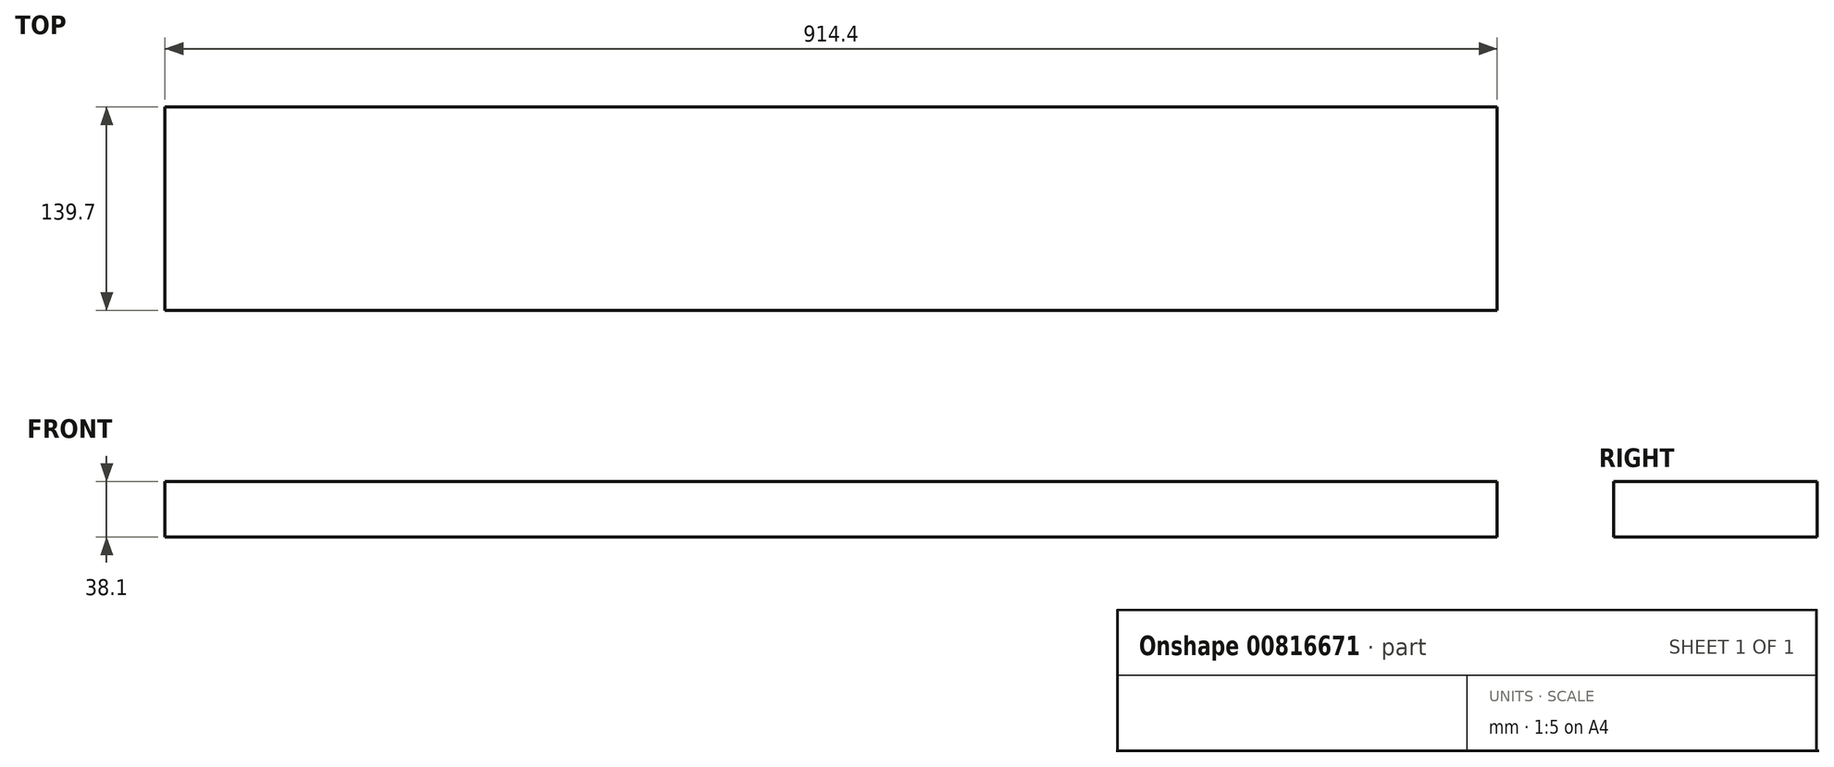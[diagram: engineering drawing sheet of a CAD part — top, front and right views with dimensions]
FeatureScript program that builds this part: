
annotation { "Feature Type Name" : "Feature", "Feature Type Description" : "" }
export const myFeature = defineFeature(function(context is Context, id is Id, definition is map)
    precondition{}
    {
        {
            var Q0;
            Q0=qCreatedBy(makeId("Top.planeOp"),FACE);
            var sketch = newSketch(context, id + "F0", { "sketchPlane" : qUnion([Q0])});
            skLineSegment(sketch, "E0.bottom", {"start": v(-755.28, 150.93) * mm, "end": v(159.12, 150.93) * mm});
            skLineSegment(sketch, "E0.top", {"start": v(-755.28, 11.23) * mm, "end": v(159.12, 11.23) * mm});
            skLineSegment(sketch, "E0.left", {"start": v(-755.28, 150.93) * mm, "end": v(-755.28, 11.23) * mm});
            skLineSegment(sketch, "E0.right", {"start": v(159.12, 150.93) * mm, "end": v(159.12, 11.23) * mm});
            skSolve(sketch);
        }
        {
            var Q0;
            Q0=makeQuery(id+"F0.imprint","IMPRINT",FACE,{"disambiguationData":[TD([[makeQuery(id+"F0.imprint","IMPRINT",EDGE,{"derivedFrom":sQuery(id+"F0.wireOp",EDGE,"E0.bottom")}),-1.0]])]});
            extrude(context, id + "F1", {"entities" : qUnion([Q0]), "depth" : 38.1 * mm, "offsetDistance" : 25.4 * mm});
        }
    });
